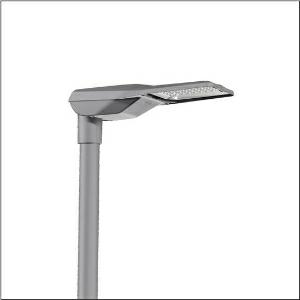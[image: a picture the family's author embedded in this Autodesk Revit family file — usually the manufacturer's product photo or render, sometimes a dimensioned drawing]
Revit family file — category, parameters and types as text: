
# Revit family: streetlight_sl_21_iq_mini___st0_8a_5xe2c31g08jb_bdc9
name_source: partatom
category: Lighting Fixtures
units: mm (PartAtom-declared; Revit-internal decimal feet)

## family parameters
Cut with Voids When Loaded = No
Host = Face
Light Source = No
Part Type = Normal
Room Calculation Point = No
Round Connector Dimension = Use Diameter
Shared = No

## types (1)
- --- (1 x LED, 10820 lm, 71.6 W, 3000K)
    Apparent Load = 72 VA
    CIE Flux Codes = 41 75 97 100 100
    Color Rendering = 70
    Color Temperature = 3000K
    Default Elevation = 1800 mm
    Description = Streetlight SL 21 iQ mini, mast luminaire, primary light control with lens, of PMMA, primary optical cover: cover, of toughened safety glass, transparent, light distribution: ST0.8a, light emission: direct distribution, primary light characteristic: asymmetric, installation type: post-top, side-entry, LED, High Power LED, rated luminous flux: 10.820lm, luminous efficacy: 151lm/W, light colour: 730, colour temperature: 3000K, control gear: iQ Street-Remote, control: Street-Remote, Auto-Match, Temp-Guard, Lumen-Switch, Night-Set, Smart-Wire, Light-Fading, Desk-Remote (wireless, voltage-free reading and setting of iQ features in the workshop via application-optimized NFC function/RFID function), optimised constant luminous flux control (CLO 2.0), pre-setting: linear dimming characteristic, mains connection: 220..240V, AC, 50/60Hz, start of lifetime: 72W, end of service life: 75W, reduction: 33W, luminaire housing, of diecast aluminium, powder-coated, SITECO metallic grey (DB 702S), corrosivity category C5 high according to DIN EN ISO 12944, please order mast flange separately, inclination adjustable: 0°, 5°, 10°, 15°, sealing non-destructively replaceable, multi-level sealing system, length: 628mm, width: 235mm, height: 110mm, mast flange for spigot size: 42mm (side-entry): 5XC10008XM4, 60/48mm (side-entry/post-top): 5XC10108XM2, 76/60mm (side-entry/post-top): 5XC10108XM1, mounting height: 4..8m, protection rating (complete): IP66, insulation class (complete): insulation class II (safety insulation), certification: CE, ENEC, ENEC+, VDE, impact resistance: IK10, permissible operating ambient temperature for outdoor applications: -40..+50°C, standard-compliant lighting for roads and squares, packaging unit: 1 piece

Light Distribution: ST0.8a
    Height = 110 mm
    Lamp = 1 x LED
    Lamp Light Flux = 10820 lm
    Lamp Power = 71.6 W
    Lamp count = 1
    Length = 625 mm
    Luminous efficacy = 151 lm/W
    Manufacturer = Siteco
    ModVariant = No
    Model = 5XE2C31G08JB
    Number of Poles = 1
    OnlyDefault = Yes
    Power Factor = 1
    Product Name = Streetlight SL 21 iQ mini | ST0.8a
    Product group = mast luminaire | pylon top
    ProductGroupID = 6100
    Protection Class = Protection class II
    Protection Degree = IP 66
    RLX_Detail_Level = 1
    RLX_Emergency_Light_Flux = 0 lm
    RLX_Emergency_Type = 0
    RLX_Emergency_Type_DB = No
    RlxData = <blob elided: 26353 chars, md5=2dcdbbd6>
    Socket = socket
    Standby Power = 0 W
    System Light Flux = 10820 lm
    System Power = 72 W
    Type Comments = factory setting: luminous flux: 100 % | dim-lin: 254 | 746 mA
    Type Image = l_1003519.jpg
    URL = http://relux.com
    VarID = @adj_168745
    Voltage = 0 V
    Weight = 0.00 kg
    Width = 234 mm

## geometry (parser evidence)
native form markers: Blend x4, Sweep x9
no freeform markers — native parametric forms only
